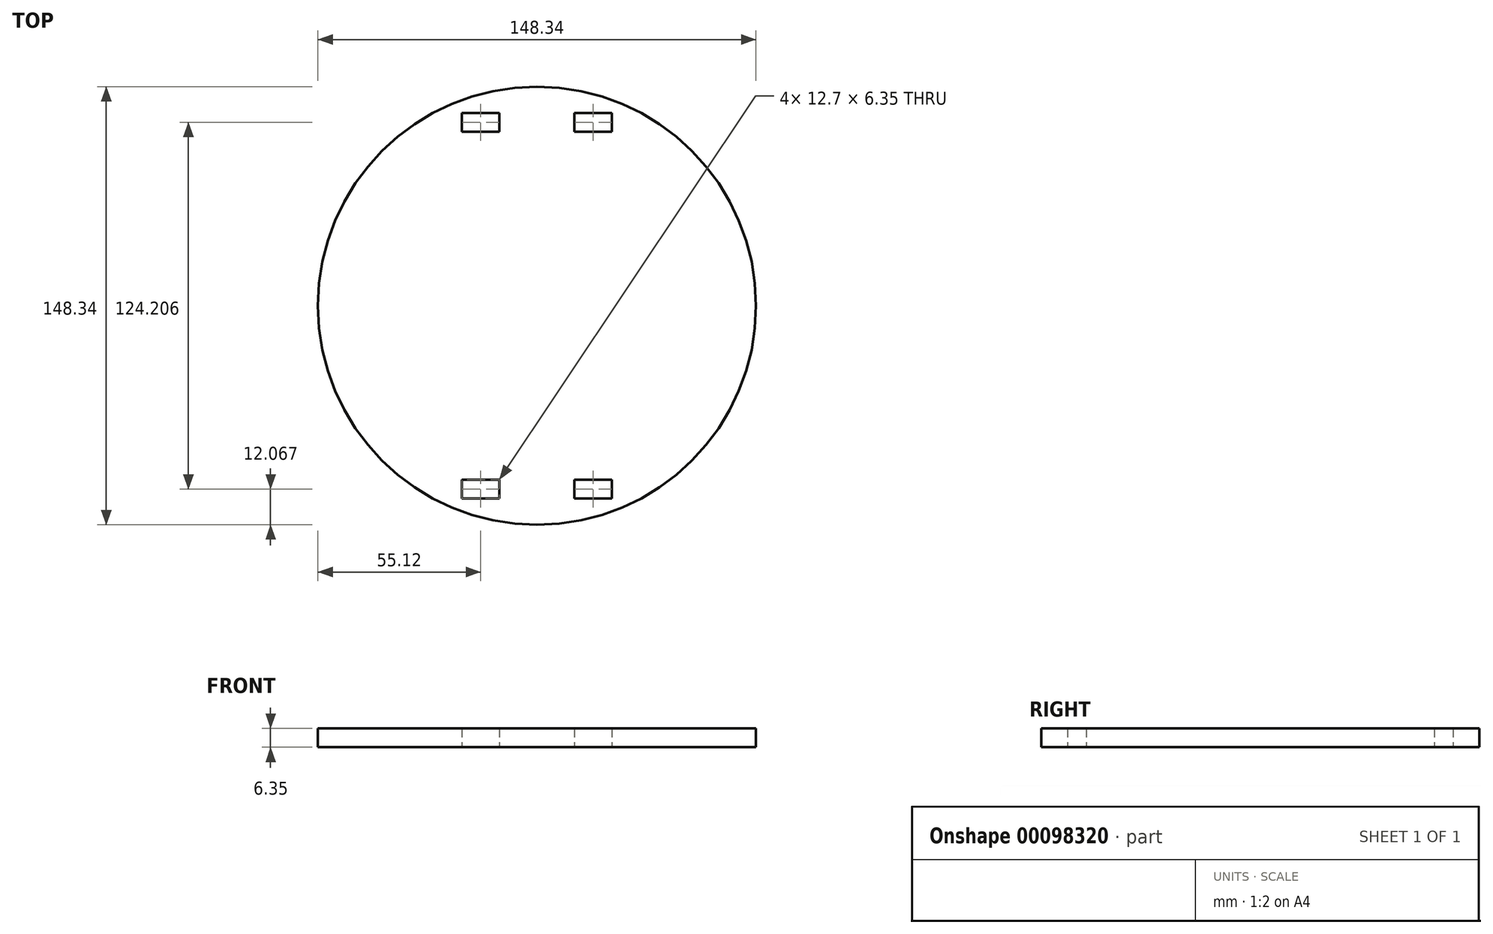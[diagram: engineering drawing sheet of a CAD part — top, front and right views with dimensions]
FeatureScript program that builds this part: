
annotation { "Feature Type Name" : "Feature", "Feature Type Description" : "" }
export const myFeature = defineFeature(function(context is Context, id is Id, definition is map)
    precondition{}
    {
        {
            var Q0;
            Q0=qCreatedBy(makeId("Top.planeOp"),FACE);
            var sketch = newSketch(context, id + "F0", { "sketchPlane" : qUnion([Q0])});
            skCircle(sketch, "E0", {"center": v(0, 0) * mm, "radius": 74.17 * mm});
            skLineSegment(sketch, "E1", {"start": v(0, -74.17) * mm, "end": v(0, -58.93) * mm});
            skLineSegment(sketch, "E2.bottom", {"start": v(-25.4, -58.93) * mm, "end": v(-12.7, -58.93) * mm});
            skLineSegment(sketch, "E2.top", {"start": v(-25.4, -65.28) * mm, "end": v(-12.7, -65.28) * mm});
            skLineSegment(sketch, "E2.left", {"start": v(-25.4, -58.93) * mm, "end": v(-25.4, -65.28) * mm});
            skLineSegment(sketch, "E2.right", {"start": v(-12.7, -58.93) * mm, "end": v(-12.7, -65.28) * mm});
            skLineSegment(sketch, "E3.bottom", {"start": v(12.7, -58.93) * mm, "end": v(25.4, -58.93) * mm});
            skLineSegment(sketch, "E3.top", {"start": v(12.7, -65.28) * mm, "end": v(25.4, -65.28) * mm});
            skLineSegment(sketch, "E3.left", {"start": v(12.7, -58.93) * mm, "end": v(12.7, -65.28) * mm});
            skLineSegment(sketch, "E3.right", {"start": v(25.4, -58.93) * mm, "end": v(25.4, -65.28) * mm});
            skLineSegment(sketch, "E4.bottom", {"start": v(25.4, 65.28) * mm, "end": v(12.7, 65.28) * mm});
            skLineSegment(sketch, "E4.top", {"start": v(25.4, 58.93) * mm, "end": v(12.7, 58.93) * mm});
            skLineSegment(sketch, "E4.left", {"start": v(25.4, 65.28) * mm, "end": v(25.4, 58.93) * mm});
            skLineSegment(sketch, "E4.right", {"start": v(12.7, 65.28) * mm, "end": v(12.7, 58.93) * mm});
            skLineSegment(sketch, "E5.bottom", {"start": v(-12.7, 65.28) * mm, "end": v(-25.4, 65.28) * mm});
            skLineSegment(sketch, "E5.top", {"start": v(-12.7, 58.93) * mm, "end": v(-25.4, 58.93) * mm});
            skLineSegment(sketch, "E5.left", {"start": v(-12.7, 65.28) * mm, "end": v(-12.7, 58.93) * mm});
            skLineSegment(sketch, "E5.right", {"start": v(-25.4, 65.28) * mm, "end": v(-25.4, 58.93) * mm});
            skSolve(sketch);
        }
        {
            var Q0;
            Q0=makeQuery(id+"F0.imprint","IMPRINT",FACE,{"disambiguationData":[TD([[makeQuery(id+"F0.imprint","IMPRINT",EDGE,{"derivedFrom":sQuery(id+"F0.wireOp",EDGE,"E0")}),1.0]])]});
            extrude(context, id + "F1", {"entities" : qUnion([Q0]), "depth" : 6.35 * mm});
        }
    });
